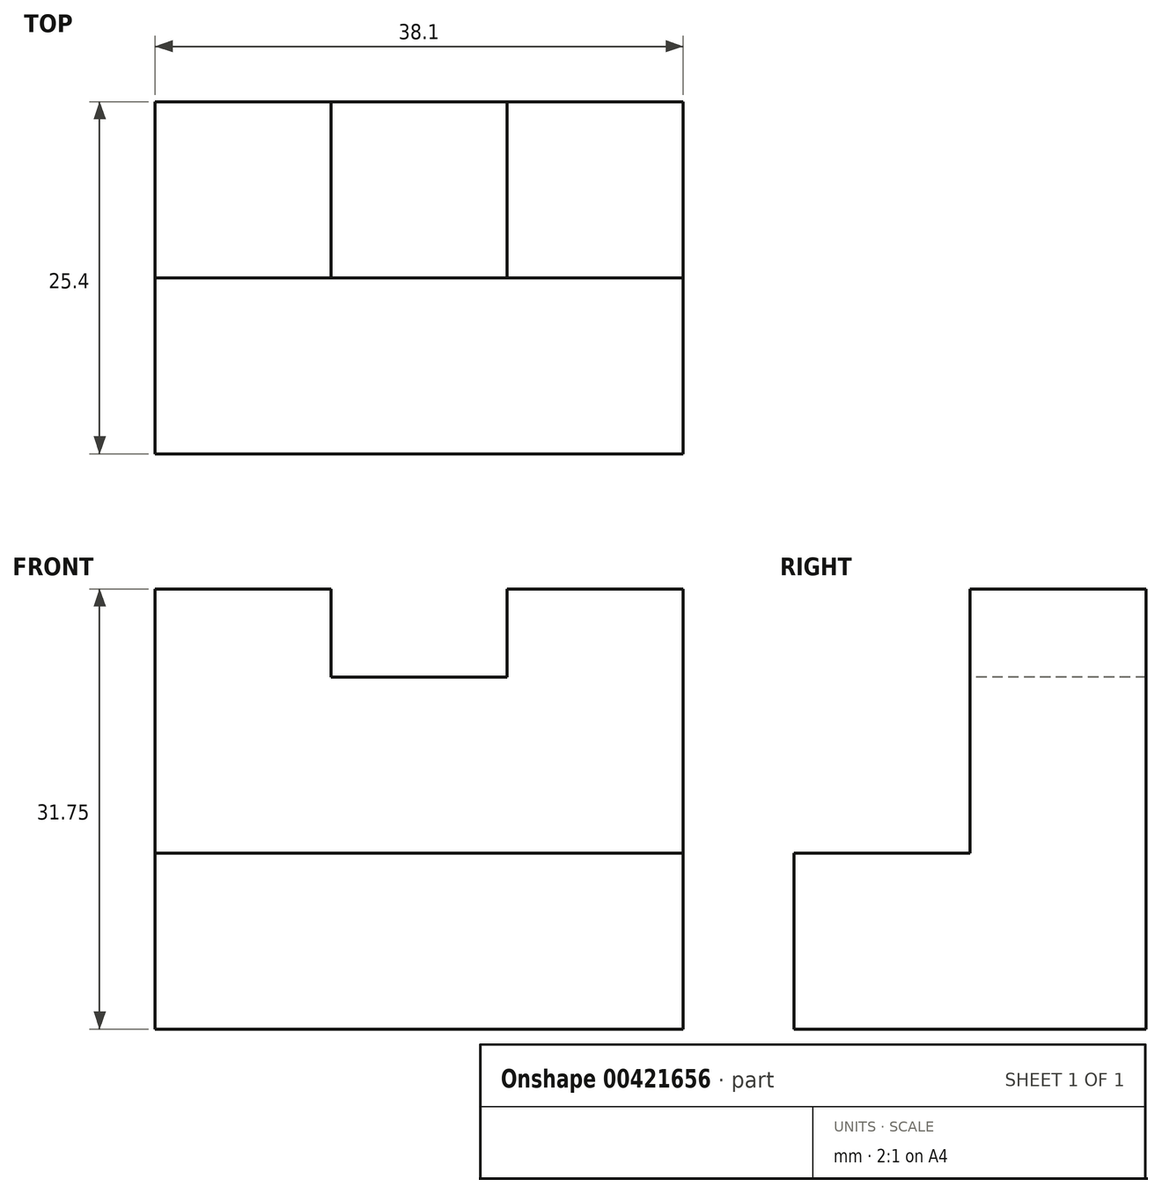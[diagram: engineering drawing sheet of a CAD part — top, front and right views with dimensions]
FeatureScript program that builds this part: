
annotation { "Feature Type Name" : "Feature", "Feature Type Description" : "" }
export const myFeature = defineFeature(function(context is Context, id is Id, definition is map)
    precondition{}
    {
        {
            var Q0;
            Q0=qCreatedBy(makeId("Top.planeOp"),FACE);
            var sketch = newSketch(context, id + "F0", { "sketchPlane" : qUnion([Q0])});
            skLineSegment(sketch, "E0", {"start": v(0, 0) * mm, "end": v(0, 12.7) * mm});
            skLineSegment(sketch, "E1", {"start": v(0, 0) * mm, "end": v(38.1, 0) * mm});
            skLineSegment(sketch, "E2", {"start": v(0, 12.7) * mm, "end": v(38.1, 12.7) * mm});
            skLineSegment(sketch, "E3", {"start": v(38.1, 12.7) * mm, "end": v(38.1, 0) * mm});
            skSolve(sketch);
        }
        {
            var Q0;
            Q0=makeQuery(id+"F0.imprint","IMPRINT",FACE,{"disambiguationData":[TD([[makeQuery(id+"F0.imprint","IMPRINT",EDGE,{"derivedFrom":sQuery(id+"F0.wireOp",EDGE,"E0")}),-1.0]])]});
            extrude(context, id + "F1", {"entities" : qUnion([Q0]), "depth" : 31.75 * mm});
        }
        {
            var Q0;
            Q0=makeQuery(id+"F1.opExtrude","CAP_FACE",FACE,{"disambiguationData":[OSD([sQuery(id+"F0.wireOp",EDGE,"E0"),sQuery(id+"F0.wireOp",EDGE,"E1"),sQuery(id+"F0.wireOp",EDGE,"E2"),sQuery(id+"F0.wireOp",EDGE,"E3")])],"isStart":false});
            var sketch = newSketch(context, id + "F2", { "sketchPlane" : qUnion([Q0])});
            skLineSegment(sketch, "E4", {"start": v(12.7, 12.7) * mm, "end": v(12.7, 0) * mm});
            skLineSegment(sketch, "E5", {"start": v(12.7, 0) * mm, "end": v(25.4, 0) * mm});
            skLineSegment(sketch, "E6", {"start": v(12.7, 12.7) * mm, "end": v(25.4, 12.7) * mm});
            skLineSegment(sketch, "E7", {"start": v(25.4, 12.7) * mm, "end": v(25.4, 0) * mm});
            skSolve(sketch);
        }
        {
            var Q0;
            Q0=makeQuery(id+"F2.imprint","IMPRINT",FACE,{"disambiguationData":[TD([[makeQuery(id+"F2.imprint","IMPRINT",EDGE,{"derivedFrom":sQuery(id+"F2.wireOp",EDGE,"E4")}),1.0]])]});
            extrude(context, id + "F3", {"entities" : qUnion([Q0]), "operationType" : NewBodyOperationType.REMOVE, "oppositeDirection" : true, "depth" : 6.35 * mm});
        }
        {
            var Q0;
            Q0=makeQuery(id+"F1.opExtrude","SWEPT_FACE",FACE,{"disambiguationData":[OSD([sQuery(id+"F0.wireOp",EDGE,"E1")])]});
            extrude(context, id + "F4", {"entities" : qUnion([Q0]), "operationType" : NewBodyOperationType.ADD, "depth" : 12.7 * mm});
        }
        {
            var Q0;
            {var subQ0=sQuery(id+"F0.wireOp",EDGE,"E3");Q0=makeQuery(id+"F4.boolean.opBoolean","MERGE",FACE,{"derivedFrom":[makeQuery(id+"F1.opExtrude","SWEPT_FACE",FACE,{"disambiguationData":[OSD([subQ0])]}),makeQuery(id+"F4.opExtrude","SWEPT_FACE",FACE,{"disambiguationData":[OSD([sQuery(id+"F0.wireOp",EDGE,"E1"),subQ0])]})]});}
            var sketch = newSketch(context, id + "F5", { "sketchPlane" : qUnion([Q0])});
            skLineSegment(sketch, "E8", {"start": v(0, 31.75) * mm, "end": v(0, 12.7) * mm});
            skPoint(sketch, "E8.endSnap0", {"position": v(0, 31.75) * mm});
            skLineSegment(sketch, "E9", {"start": v(0, 12.7) * mm, "end": v(-12.7, 12.7) * mm});
            skLineSegment(sketch, "E10", {"start": v(-12.7, 12.7) * mm, "end": v(-12.7, 31.75) * mm});
            skLineSegment(sketch, "E11", {"start": v(-12.7, 31.75) * mm, "end": v(0, 31.75) * mm});
            skSolve(sketch);
        }
        {
            var Q0;
            Q0=makeQuery(id+"F5.imprint","IMPRINT",FACE,{"disambiguationData":[TD([[makeQuery(id+"F5.imprint","IMPRINT",EDGE,{"derivedFrom":sQuery(id+"F5.wireOp",EDGE,"E8")}),-1.0]])]});
            extrude(context, id + "F6", {"entities" : qUnion([Q0]), "operationType" : NewBodyOperationType.REMOVE, "oppositeDirection" : true, "depth" : 25.4 * mm});
        }
        {
            var Q0;
            {var subQ0=sQuery(id+"F0.wireOp",EDGE,"E0");Q0=makeQuery(id+"F4.boolean.opBoolean","MERGE",FACE,{"derivedFrom":[makeQuery(id+"F1.opExtrude","SWEPT_FACE",FACE,{"disambiguationData":[OSD([subQ0])]}),makeQuery(id+"F4.opExtrude","SWEPT_FACE",FACE,{"disambiguationData":[OSD([subQ0,sQuery(id+"F0.wireOp",EDGE,"E1")])]})]});}
            var sketch = newSketch(context, id + "F7", { "sketchPlane" : qUnion([Q0])});
            skLineSegment(sketch, "E12", {"start": v(0, 31.75) * mm, "end": v(0, 12.7) * mm});
            skPoint(sketch, "E12.endSnap0", {"position": v(0, 31.75) * mm});
            skLineSegment(sketch, "E13", {"start": v(0, 12.7) * mm, "end": v(12.7, 12.7) * mm});
            skLineSegment(sketch, "E14", {"start": v(0, 31.75) * mm, "end": v(12.7, 31.75) * mm});
            skLineSegment(sketch, "E15", {"start": v(12.7, 31.75) * mm, "end": v(12.7, 12.7) * mm});
            skSolve(sketch);
        }
        {
            var Q0;
            Q0=makeQuery(id+"F7.imprint","IMPRINT",FACE,{"disambiguationData":[TD([[makeQuery(id+"F7.imprint","IMPRINT",EDGE,{"derivedFrom":sQuery(id+"F7.wireOp",EDGE,"E12")}),1.0]])]});
            extrude(context, id + "F8", {"entities" : qUnion([Q0]), "operationType" : NewBodyOperationType.REMOVE, "oppositeDirection" : true, "depth" : 25.4 * mm});
        }
    });
